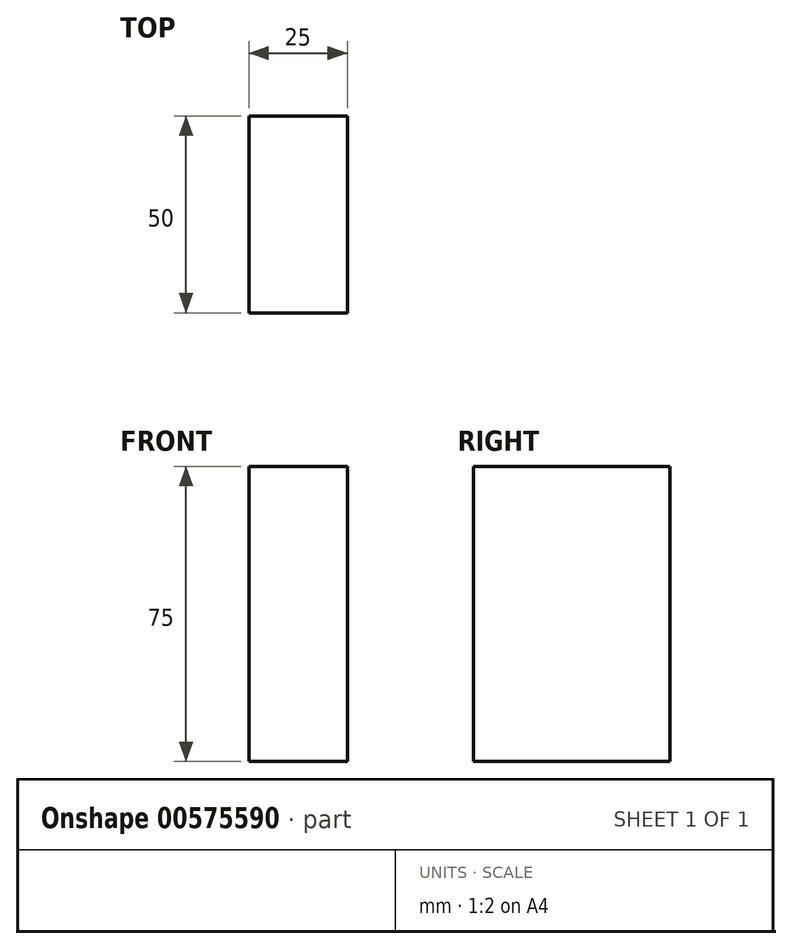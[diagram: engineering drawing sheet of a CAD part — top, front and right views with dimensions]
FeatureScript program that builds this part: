
annotation { "Feature Type Name" : "Feature", "Feature Type Description" : "" }
export const myFeature = defineFeature(function(context is Context, id is Id, definition is map)
    precondition{}
    {
        {
            var Q0;
            Q0=qCreatedBy(makeId("Top.planeOp"),FACE);
            var sketch = newSketch(context, id + "F0", { "sketchPlane" : qUnion([Q0])});
            skLineSegment(sketch, "E0.bottom", {"start": v(-29.2, 32.3) * mm, "end": v(-4.2, 32.3) * mm});
            skLineSegment(sketch, "E0.top", {"start": v(-29.2, -17.7) * mm, "end": v(-4.2, -17.7) * mm});
            skLineSegment(sketch, "E0.left", {"start": v(-29.2, 32.3) * mm, "end": v(-29.2, -17.7) * mm});
            skLineSegment(sketch, "E0.right", {"start": v(-4.2, 32.3) * mm, "end": v(-4.2, -17.7) * mm});
            skSolve(sketch);
        }
        {
            var Q0;
            Q0=makeQuery(id+"F0.imprint","IMPRINT",FACE,{"disambiguationData":[TD([[makeQuery(id+"F0.imprint","IMPRINT",EDGE,{"derivedFrom":sQuery(id+"F0.wireOp",EDGE,"E0.bottom")}),-1.0]])]});
            extrude(context, id + "F1", {"entities" : qUnion([Q0]), "depth" : 75 * mm, "offsetDistance" : 25 * mm});
        }
    });
